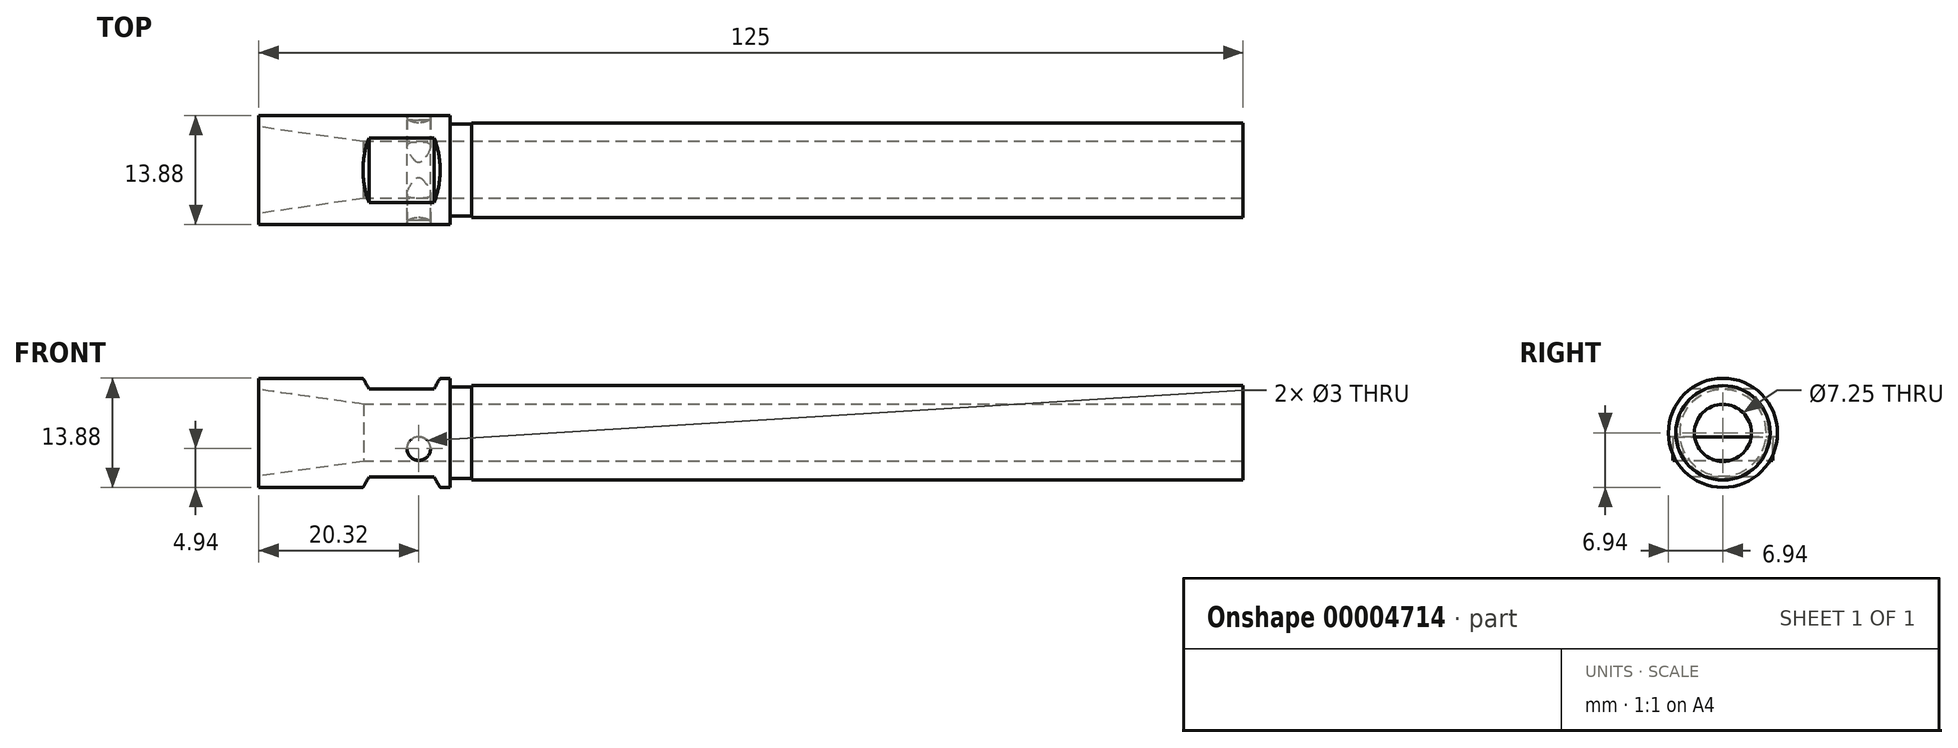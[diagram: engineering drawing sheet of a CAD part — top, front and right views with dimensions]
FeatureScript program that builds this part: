
annotation { "Feature Type Name" : "Feature", "Feature Type Description" : "" }
export const myFeature = defineFeature(function(context is Context, id is Id, definition is map)
    precondition{}
    {
        {
            var Q0;
            Q0=qCreatedBy(makeId("Front.planeOp"),FACE);
            var sketch = newSketch(context, id + "F0", { "sketchPlane" : qUnion([Q0])});
            skLineSegment(sketch, "E0", {"start": v(-20.32, 8.93) * mm, "end": v(3.98, 8.93) * mm});
            skLineSegment(sketch, "E1", {"start": v(-20.32, 7.5) * mm, "end": v(-20.32, 8.93) * mm});
            skLineSegment(sketch, "E2", {"start": v(-20.32, 7.5) * mm, "end": v(-6.98, 5.62) * mm});
            skLineSegment(sketch, "E3", {"start": v(-6.98, 5.62) * mm, "end": v(104.68, 5.62) * mm});
            skLineSegment(sketch, "E4", {"start": v(3.98, 7.83) * mm, "end": v(3.98, 8.93) * mm});
            skLineSegment(sketch, "E5", {"start": v(104.68, 8) * mm, "end": v(104.68, 5.62) * mm});
            skLineSegment(sketch, "E6", {"start": v(-57.42, 2) * mm, "end": v(66.28, 2) * mm, "construction": true});
            skLineSegment(sketch, "E7", {"start": v(3.98, 7.83) * mm, "end": v(6.68, 7.83) * mm});
            skLineSegment(sketch, "E8", {"start": v(6.68, 7.83) * mm, "end": v(6.68, 8) * mm});
            skLineSegment(sketch, "E9", {"start": v(6.68, 8) * mm, "end": v(104.68, 8) * mm});
            skLineSegment(sketch, "E10.MirrorCS", {"start": v(6.68, -3.83) * mm, "end": v(6.68, -4) * mm});
            skLineSegment(sketch, "E11.MirrorCS", {"start": v(3.98, -3.83) * mm, "end": v(3.98, -4.93) * mm});
            skLineSegment(sketch, "E12.MirrorCS", {"start": v(3.98, -3.83) * mm, "end": v(6.68, -3.83) * mm});
            skLineSegment(sketch, "E13.MirrorCS", {"start": v(-20.32, -3.5) * mm, "end": v(-20.32, -4.94) * mm});
            skLineSegment(sketch, "E14.MirrorCS", {"start": v(-20.32, -3.5) * mm, "end": v(-6.98, -1.62) * mm});
            skLineSegment(sketch, "E15.MirrorCS", {"start": v(-6.98, -1.62) * mm, "end": v(104.68, -1.62) * mm});
            skLineSegment(sketch, "E16.MirrorCS", {"start": v(104.68, -4) * mm, "end": v(104.68, -1.62) * mm});
            skLineSegment(sketch, "E17.MirrorCS", {"start": v(6.68, -4) * mm, "end": v(104.68, -4) * mm});
            skLineSegment(sketch, "E18.MirrorCS", {"start": v(-20.32, -4.93) * mm, "end": v(3.98, -4.93) * mm});
            skLineSegment(sketch, "E19", {"start": v(-6.98, 5.63) * mm, "end": v(18.81, 2) * mm, "construction": true});
            skCircle(sketch, "E20", {"center": v(0, 0) * mm, "radius": 1.5 * mm});
            skSolve(sketch);
        }
        {
            var Q0;
            Q0=makeQuery(id+"F0.imprint","IMPRINT",FACE,{"disambiguationData":[TD([[makeQuery(id+"F0.imprint","IMPRINT",EDGE,{"derivedFrom":sQuery(id+"F0.wireOp",EDGE,"E0")}),-1.0]])]});
            var Q1;
            Q1=sQuery(id+"F0.wireOp",EDGE,"E6");
            revolve(context, id + "F1", {"entities" : qUnion([Q0]), "axis" : qUnion([Q1]), "revolveType" : RevolveType.FULL});
        }
        {
            var Q0;
            Q0=qCreatedBy(makeId("Front.planeOp"),FACE);
            var sketch = newSketch(context, id + "F2", { "sketchPlane" : qUnion([Q0])});
            skLineSegment(sketch, "E21.bottom", {"start": v(-7.47, 9.6) * mm, "end": v(3.08, 9.6) * mm});
            skLineSegment(sketch, "E21.top", {"start": v(-6.32, 7.6) * mm, "end": v(1.93, 7.6) * mm});
            skLineSegment(sketch, "E21.left", {"start": v(-7.47, 9.6) * mm, "end": v(-6.32, 7.6) * mm});
            skLineSegment(sketch, "E21.right", {"start": v(3.08, 9.6) * mm, "end": v(1.93, 7.6) * mm});
            skLineSegment(sketch, "E22.MirrorCS", {"start": v(3.08, -5.6) * mm, "end": v(1.93, -3.6) * mm});
            skLineSegment(sketch, "E23.MirrorCS", {"start": v(-7.47, -5.6) * mm, "end": v(-6.32, -3.6) * mm});
            skLineSegment(sketch, "E24.MirrorCS", {"start": v(-7.47, -5.6) * mm, "end": v(3.08, -5.6) * mm});
            skLineSegment(sketch, "E25.MirrorCS", {"start": v(-6.32, -3.6) * mm, "end": v(1.93, -3.6) * mm});
            skSolve(sketch);
        }
        {
            var Q0;
            Q0=makeQuery(id+"F2.imprint","IMPRINT",FACE,{"disambiguationData":[TD([[makeQuery(id+"F2.imprint","IMPRINT",EDGE,{"derivedFrom":sQuery(id+"F2.wireOp",EDGE,"E21.bottom")}),-1.0]])]});
            var Q1;
            Q1=makeQuery(id+"F2.imprint","IMPRINT",FACE,{"disambiguationData":[TD([[makeQuery(id+"F2.imprint","IMPRINT",EDGE,{"derivedFrom":sQuery(id+"F2.wireOp",EDGE,"E22.MirrorCS")}),1.0]])]});
            extrude(context, id + "F3", {"entities" : qUnion([Q0, Q1]), "operationType" : NewBodyOperationType.REMOVE, "endBound" : BoundingType.SYMMETRIC, "oppositeDirection" : true, "depth" : 25.4 * mm});
        }
        {
            var Q0;
            Q0=makeQuery(id+"F0.imprint","IMPRINT",FACE,{"disambiguationData":[TD([[makeQuery(id+"F0.imprint","IMPRINT",EDGE,{"derivedFrom":sQuery(id+"F0.wireOp",EDGE,"E20")}),1.0]])]});
            extrude(context, id + "F4", {"entities" : qUnion([Q0]), "operationType" : NewBodyOperationType.REMOVE, "endBound" : BoundingType.SYMMETRIC, "oppositeDirection" : true, "depth" : 15.24 * mm});
        }
        {
            var Q0;
            Q0=makeQuery(id+"F0.imprint","IMPRINT",FACE,{"disambiguationData":[TD([[makeQuery(id+"F0.imprint","IMPRINT",EDGE,{"derivedFrom":sQuery(id+"F0.wireOp",EDGE,"E20")}),1.0]])]});
            extrude(context, id + "F5", {"entities" : qUnion([Q0]), "endBound" : BoundingType.SYMMETRIC, "depth" : 12.7 * mm});
        }
    });
